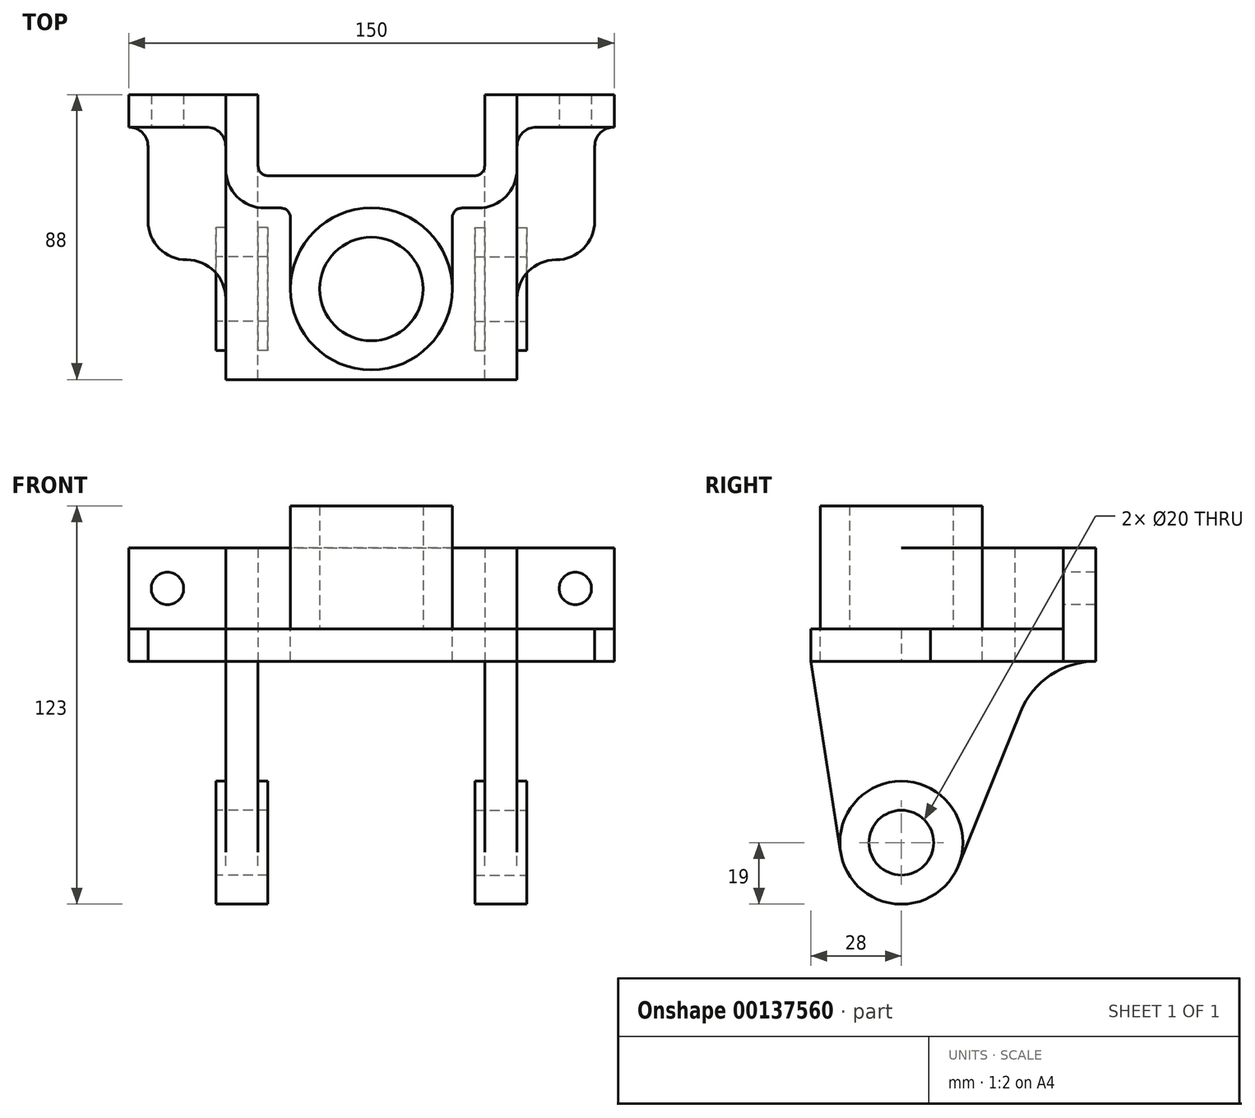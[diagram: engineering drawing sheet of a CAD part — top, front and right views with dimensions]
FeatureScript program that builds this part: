
annotation { "Feature Type Name" : "Feature", "Feature Type Description" : "" }
export const myFeature = defineFeature(function(context is Context, id is Id, definition is map)
    precondition{}
    {
        {
            var Q0;
            Q0=qCreatedBy(makeId("Top.planeOp"),FACE);
            var sketch = newSketch(context, id + "F0", { "sketchPlane" : qUnion([Q0])});
            skCircle(sketch, "E0", {"center": v(0, 0) * mm, "radius": 16 * mm});
            skCircle(sketch, "E1", {"center": v(0, 0) * mm, "radius": 25 * mm});
            skSolve(sketch);
        }
        {
            var Q0;
            Q0 = qSketchRegion(id + "F0", true);
            extrude(context, id + "F1", {"entities" : qUnion([Q0]), "depth" : 38 * mm});
        }
        {
            var Q0;
            Q0=qCreatedBy(makeId("Top.planeOp"),FACE);
            var sketch = newSketch(context, id + "F2", { "sketchPlane" : qUnion([Q0])});
            skLineSegment(sketch, "E2", {"start": v(-75, 60) * mm, "end": v(-35, 60) * mm});
            skLineSegment(sketch, "E3", {"start": v(-75, 60) * mm, "end": v(-75, 50) * mm});
            skLineSegment(sketch, "E4", {"start": v(-75, 50) * mm, "end": v(-45, 50) * mm});
            skLineSegment(sketch, "E5", {"start": v(-35, 35) * mm, "end": v(0, 35) * mm});
            skLineSegment(sketch, "E6", {"start": v(-25, 0) * mm, "end": v(-25, 25) * mm});
            skLineSegment(sketch, "E7", {"start": v(-35, 60) * mm, "end": v(-35, 35) * mm});
            skLineSegment(sketch, "E8", {"start": v(-45, 50) * mm, "end": v(-45, 25) * mm});
            skLineSegment(sketch, "E9", {"start": v(-45, 25) * mm, "end": v(-25, 25) * mm});
            skLineSegment(sketch, "E10", {"start": v(0, 56.78) * mm, "end": v(0, -59.54) * mm, "construction": true});
            skLineSegment(sketch, "E11", {"start": v(-57.64, 0) * mm, "end": v(65.58, 0) * mm, "construction": true});
            skLineSegment(sketch, "E12.MirrorCS", {"start": v(75, 60) * mm, "end": v(35, 60) * mm});
            skLineSegment(sketch, "E13.MirrorCS", {"start": v(75, 60) * mm, "end": v(75, 50) * mm});
            skLineSegment(sketch, "E14.MirrorCS", {"start": v(75, 50) * mm, "end": v(45, 50) * mm});
            skLineSegment(sketch, "E15.MirrorCS", {"start": v(35, 60) * mm, "end": v(35, 35) * mm});
            skLineSegment(sketch, "E16.MirrorCS", {"start": v(45, 50) * mm, "end": v(45, 25) * mm});
            skLineSegment(sketch, "E17.MirrorCS", {"start": v(45, 25) * mm, "end": v(25, 25) * mm});
            skLineSegment(sketch, "E18.MirrorCS", {"start": v(35, 35) * mm, "end": v(0, 35) * mm});
            skLineSegment(sketch, "E19.MirrorCS", {"start": v(25, 0) * mm, "end": v(25, 25) * mm});
            skArc(sketch, "E20.0", {"start": v(25, 0) * mm, "mid": v(0, 25) * mm, "end": v(-25, 0) * mm});
            skSolve(sketch);
        }
        {
            var Q0;
            Q0 = qSketchRegion(id + "F2", true);
            extrude(context, id + "F3", {"entities" : qUnion([Q0]), "operationType" : NewBodyOperationType.ADD, "depth" : 25 * mm, "hasSecondDirection" : true, "secondDirectionOppositeDirection" : true, "secondDirectionDepth" : 10 * mm});
        }
        {
            var Q0;
            Q0=makeQuery(id+"F3.opExtrude","SWEPT_EDGE",EDGE,{"disambiguationData":[OSD([sQuery(id+"F2.wireOp",EDGE,"E14.MirrorCS"),sQuery(id+"F2.wireOp",EDGE,"E16.MirrorCS")])]});
            var Q1;
            Q1=makeQuery(id+"F3.opExtrude","SWEPT_EDGE",EDGE,{"disambiguationData":[OSD([sQuery(id+"F2.wireOp",EDGE,"E4"),sQuery(id+"F2.wireOp",EDGE,"E8")])]});
            fillet(context, id + "F4", {"entities" : qUnion([Q0, Q1]), "radius" : 6 * mm, "tangentPropagation" : true, "allowEdgeOverflow" : false});
        }
        {
            var Q0;
            Q0=makeQuery(id+"F3.opExtrude","SWEPT_EDGE",EDGE,{"disambiguationData":[OSD([sQuery(id+"F2.wireOp",EDGE,"E17.MirrorCS"),sQuery(id+"F2.wireOp",EDGE,"E19.MirrorCS")])]});
            var Q1;
            Q1=makeQuery(id+"F3.opExtrude","SWEPT_EDGE",EDGE,{"disambiguationData":[OSD([sQuery(id+"F2.wireOp",EDGE,"E6"),sQuery(id+"F2.wireOp",EDGE,"E9")])]});
            var Q2;
            Q2=makeQuery(id+"F3.opExtrude","SWEPT_EDGE",EDGE,{"disambiguationData":[OSD([sQuery(id+"F2.wireOp",EDGE,"E5"),sQuery(id+"F2.wireOp",EDGE,"E7")])]});
            var Q3;
            Q3=makeQuery(id+"F3.opExtrude","SWEPT_EDGE",EDGE,{"disambiguationData":[OSD([sQuery(id+"F2.wireOp",EDGE,"E15.MirrorCS"),sQuery(id+"F2.wireOp",EDGE,"E18.MirrorCS")])]});
            fillet(context, id + "F5", {"entities" : qUnion([Q0, Q1, Q2, Q3]), "radius" : 3 * mm, "tangentPropagation" : true, "allowEdgeOverflow" : false});
        }
        {
            var Q0;
            Q0=makeQuery(id+"F3.opExtrude","SWEPT_EDGE",EDGE,{"disambiguationData":[OSD([sQuery(id+"F2.wireOp",EDGE,"E8"),sQuery(id+"F2.wireOp",EDGE,"E9")])]});
            var Q1;
            Q1=makeQuery(id+"F3.opExtrude","SWEPT_EDGE",EDGE,{"disambiguationData":[OSD([sQuery(id+"F2.wireOp",EDGE,"E16.MirrorCS"),sQuery(id+"F2.wireOp",EDGE,"E17.MirrorCS")])]});
            fillet(context, id + "F6", {"entities" : qUnion([Q0, Q1]), "radius" : 12 * mm, "tangentPropagation" : true, "allowEdgeOverflow" : false});
        }
        {
            var Q0;
            Q0=qCreatedBy(makeId("Top.planeOp"),FACE);
            var sketch = newSketch(context, id + "F7", { "sketchPlane" : qUnion([Q0])});
            skLineSegment(sketch, "E21", {"start": v(0, -28) * mm, "end": v(45, -28) * mm});
            skLineSegment(sketch, "E22.0", {"start": v(75, 50) * mm, "end": v(51, 50) * mm});
            skArc(sketch, "E23", {"start": v(75, 50) * mm, "mid": v(70.76, 48.24) * mm, "end": v(69, 44) * mm});
            skLineSegment(sketch, "E24", {"start": v(69, 44) * mm, "end": v(69, 9) * mm});
            skLineSegment(sketch, "E25", {"start": v(45, -28) * mm, "end": v(45, 9) * mm});
            skLineSegment(sketch, "E26", {"start": v(69, 9) * mm, "end": v(45, 9) * mm});
            skLineSegment(sketch, "E27", {"start": v(0, 64.57) * mm, "end": v(0, -62.74) * mm, "construction": true});
            skPoint(sketch, "E27.endSnap0", {"position": v(0, -28) * mm});
            skPoint(sketch, "E28.orphan", {"position": v(-45, -28) * mm});
            skLineSegment(sketch, "E29.MirrorCS", {"start": v(0, -28) * mm, "end": v(-45, -28) * mm});
            skLineSegment(sketch, "E30.MirrorCS", {"start": v(-45, -28) * mm, "end": v(-45, 9) * mm});
            skLineSegment(sketch, "E31.MirrorCS", {"start": v(-69, 9) * mm, "end": v(-45, 9) * mm});
            skLineSegment(sketch, "E32.MirrorCS", {"start": v(-69, 44) * mm, "end": v(-69, 9) * mm});
            skArc(sketch, "E33.MirrorCS", {"start": v(-75, 50) * mm, "mid": v(-70.76, 48.24) * mm, "end": v(-69, 44) * mm});
            skLineSegment(sketch, "E34.0", {"start": v(-75, 50) * mm, "end": v(-51, 50) * mm});
            skLineSegment(sketch, "E35.0", {"start": v(-45, 44) * mm, "end": v(-45, 37) * mm});
            skLineSegment(sketch, "E36.0", {"start": v(-33, 25) * mm, "end": v(-28, 25) * mm});
            skLineSegment(sketch, "E37.0", {"start": v(-25, 0) * mm, "end": v(-25, 22) * mm});
            skLineSegment(sketch, "E38.0", {"start": v(25, 0) * mm, "end": v(25, 22) * mm});
            skLineSegment(sketch, "E39.0", {"start": v(33, 25) * mm, "end": v(28, 25) * mm});
            skLineSegment(sketch, "E40.0", {"start": v(45, 44) * mm, "end": v(45, 37) * mm});
            skArc(sketch, "E41.0", {"start": v(-25, 0) * mm, "mid": v(0, -25) * mm, "end": v(25, 0) * mm});
            skArc(sketch, "E42.0", {"start": v(45, 44) * mm, "mid": v(46.76, 48.24) * mm, "end": v(51, 50) * mm});
            skArc(sketch, "E43.0", {"start": v(25, 22) * mm, "mid": v(25.88, 24.12) * mm, "end": v(28, 25) * mm});
            skArc(sketch, "E44.0", {"start": v(-28, 25) * mm, "mid": v(-25.88, 24.12) * mm, "end": v(-25, 22) * mm});
            skArc(sketch, "E45.0", {"start": v(-51, 50) * mm, "mid": v(-46.76, 48.24) * mm, "end": v(-45, 44) * mm});
            skPoint(sketch, "E46.orphan", {"position": v(-45, 50) * mm});
            skPoint(sketch, "E47.orphan", {"position": v(-25, 25) * mm});
            skPoint(sketch, "E48.orphan", {"position": v(25, 25) * mm});
            skPoint(sketch, "E49.orphan", {"position": v(45, 50) * mm});
            skArc(sketch, "E50.0", {"start": v(-45, 37) * mm, "mid": v(-41.49, 28.51) * mm, "end": v(-33, 25) * mm});
            skArc(sketch, "E51.0", {"start": v(33, 25) * mm, "mid": v(41.49, 28.51) * mm, "end": v(45, 37) * mm});
            skSolve(sketch);
        }
        {
            var Q0;
            Q0 = qSketchRegion(id + "F7", true);
            extrude(context, id + "F8", {"entities" : qUnion([Q0]), "oppositeDirection" : true, "depth" : 10 * mm});
        }
        {
            var Q0;
            Q0=makeQuery(id+"F8.opExtrude","SWEPT_EDGE",EDGE,{"disambiguationData":[OSD([sQuery(id+"F7.wireOp",EDGE,"E31.MirrorCS"),sQuery(id+"F7.wireOp",EDGE,"E32.MirrorCS")])]});
            var Q1;
            Q1=makeQuery(id+"F8.opExtrude","SWEPT_EDGE",EDGE,{"disambiguationData":[OSD([sQuery(id+"F7.wireOp",EDGE,"E30.MirrorCS"),sQuery(id+"F7.wireOp",EDGE,"E31.MirrorCS")])]});
            var Q2;
            Q2=makeQuery(id+"F8.opExtrude","SWEPT_EDGE",EDGE,{"disambiguationData":[OSD([sQuery(id+"F7.wireOp",EDGE,"E25"),sQuery(id+"F7.wireOp",EDGE,"E26")])]});
            var Q3;
            Q3=makeQuery(id+"F8.opExtrude","SWEPT_EDGE",EDGE,{"disambiguationData":[OSD([sQuery(id+"F7.wireOp",EDGE,"E24"),sQuery(id+"F7.wireOp",EDGE,"E26")])]});
            fillet(context, id + "F9", {"entities" : qUnion([Q0, Q1, Q2, Q3]), "radius" : 12 * mm, "tangentPropagation" : true, "allowEdgeOverflow" : false});
        }
        {
            var Q0;
            Q0=makeQuery(id+"F8.opExtrude","SWEPT_FACE",FACE,{"disambiguationData":[OSD([sQuery(id+"F7.wireOp",EDGE,"E25")])]});
            var sketch = newSketch(context, id + "F10", { "sketchPlane" : qUnion([Q0])});
            skArc(sketch, "E52", {"start": v(-18.77, -68.94) * mm, "mid": v(-2.17, -84.88) * mm, "end": v(17.61, -73.12) * mm});
            skLineSegment(sketch, "E53.0", {"start": v(-28, -10) * mm, "end": v(-3, -10) * mm});
            skLineSegment(sketch, "E54", {"start": v(-28, -10) * mm, "end": v(-18.77, -68.94) * mm});
            skArc(sketch, "E55", {"start": v(60, -10) * mm, "mid": v(46.02, -14.27) * mm, "end": v(36.82, -25.63) * mm});
            skLineSegment(sketch, "E56", {"start": v(17.61, -73.12) * mm, "end": v(36.82, -25.63) * mm});
            skLineSegment(sketch, "E57.0", {"start": v(9, -10) * mm, "end": v(-3, -10) * mm});
            skLineSegment(sketch, "E58.0", {"start": v(21, -10) * mm, "end": v(9, -10) * mm});
            skLineSegment(sketch, "E59.0", {"start": v(44, -10) * mm, "end": v(21, -10) * mm});
            skLineSegment(sketch, "E60.0", {"start": v(50, -10) * mm, "end": v(44, -10) * mm});
            skLineSegment(sketch, "E61.0", {"start": v(60, -10) * mm, "end": v(50, -10) * mm});
            skSolve(sketch);
        }
        {
            var Q0;
            Q0 = qSketchRegion(id + "F10", true);
            extrude(context, id + "F11", {"entities" : qUnion([Q0]), "oppositeDirection" : true, "depth" : 10 * mm});
        }
        {
            var Q0;
            Q0=makeQuery(id+"F11.opExtrude","CAP_FACE",FACE,{"disambiguationData":[OSD([sQuery(id+"F10.wireOp",EDGE,"E52"),sQuery(id+"F10.wireOp",EDGE,"E53.0"),sQuery(id+"F10.wireOp",EDGE,"E54"),sQuery(id+"F10.wireOp",EDGE,"E55"),sQuery(id+"F10.wireOp",EDGE,"E56"),sQuery(id+"F10.wireOp",EDGE,"E57.0"),sQuery(id+"F10.wireOp",EDGE,"E58.0"),sQuery(id+"F10.wireOp",EDGE,"E59.0"),sQuery(id+"F10.wireOp",EDGE,"E60.0"),sQuery(id+"F10.wireOp",EDGE,"E61.0")])],"isStart":true});
            var sketch = newSketch(context, id + "F12", { "sketchPlane" : qUnion([Q0])});
            skCircle(sketch, "E62", {"center": v(0, -66) * mm, "radius": 19 * mm});
            skSolve(sketch);
        }
        {
            var Q0;
            Q0 = qSketchRegion(id + "F12", true);
            extrude(context, id + "F13", {"entities" : qUnion([Q0]), "depth" : 3 * mm});
        }
        {
            var Q0;
            Q0=makeQuery(id+"F13.opExtrude","CAP_FACE",FACE,{"disambiguationData":[OSD([sQuery(id+"F12.wireOp",EDGE,"E62")])],"isStart":false});
            cPlane(context, id + "F14", {"entities" : qUnion([Q0]), "cplaneType" : CPlaneType.OFFSET, "offset" : 8 * mm, "oppositeDirection" : true, "width" : 150 * mm, "height" : 150 * mm});
        }
        {
            var Q0;
            Q0=makeQuery(id+"F13.opExtrude","SWEPT_BODY",BODY,{"disambiguationData":[OSD([sQuery(id+"F12.wireOp",EDGE,"E62")])]});
            var Q1;
            Q1=qCreatedBy(id+"F14.planeOp",FACE);
            mirror(context, id + "F15", {"operationType" : NewBodyOperationType.ADD, "entities" : qUnion([Q0]), "mirrorPlane" : qUnion([Q1])});
        }
        {
            var Q0;
            Q0=makeQuery(id+"F13.opExtrude","CAP_FACE",FACE,{"disambiguationData":[OSD([sQuery(id+"F12.wireOp",EDGE,"E62")])],"isStart":false});
            var sketch = newSketch(context, id + "F16", { "sketchPlane" : qUnion([Q0])});
            skPoint(sketch, "E63", {"position": v(0, -66) * mm});
            skSolve(sketch);
        }
        {
            var Q0;
            Q0=sQuery(id+"F16.wireOp",VERTEX,"E63");
            var Q1;
            Q1=makeQuery(id+"F11.opExtrude","SWEPT_BODY",BODY,{"disambiguationData":[OSD([sQuery(id+"F10.wireOp",EDGE,"E52"),sQuery(id+"F10.wireOp",EDGE,"E53.0"),sQuery(id+"F10.wireOp",EDGE,"E54"),sQuery(id+"F10.wireOp",EDGE,"E55"),sQuery(id+"F10.wireOp",EDGE,"E56"),sQuery(id+"F10.wireOp",EDGE,"E57.0"),sQuery(id+"F10.wireOp",EDGE,"E58.0"),sQuery(id+"F10.wireOp",EDGE,"E59.0"),sQuery(id+"F10.wireOp",EDGE,"E60.0"),sQuery(id+"F10.wireOp",EDGE,"E61.0")])]});
            hole(context, id + "F17", {"style" : HoleStyle.SIMPLE, "endStyle" : HoleEndStyle.BLIND, "holeDiameter" : 20 * mm, "holeDepth" : 25 * mm, "locations" : qUnion([Q0]), "scope" : qUnion([Q1])});
        }
        {
            var Q0;
            Q0=makeQuery(id+"F11.opExtrude","SWEPT_BODY",BODY,{"disambiguationData":[OSD([sQuery(id+"F10.wireOp",EDGE,"E52"),sQuery(id+"F10.wireOp",EDGE,"E53.0"),sQuery(id+"F10.wireOp",EDGE,"E54"),sQuery(id+"F10.wireOp",EDGE,"E55"),sQuery(id+"F10.wireOp",EDGE,"E56"),sQuery(id+"F10.wireOp",EDGE,"E57.0"),sQuery(id+"F10.wireOp",EDGE,"E58.0"),sQuery(id+"F10.wireOp",EDGE,"E59.0"),sQuery(id+"F10.wireOp",EDGE,"E60.0"),sQuery(id+"F10.wireOp",EDGE,"E61.0")])]});
            var Q1;
            Q1=qCreatedBy(makeId("Right.planeOp"),FACE);
            mirror(context, id + "F18", {"entities" : qUnion([Q0]), "mirrorPlane" : qUnion([Q1])});
        }
        {
            var Q0;
            Q0=makeQuery(id+"F3.opExtrude","SWEPT_FACE",FACE,{"disambiguationData":[OSD([sQuery(id+"F2.wireOp",EDGE,"E14.MirrorCS")])]});
            var sketch = newSketch(context, id + "F19", { "sketchPlane" : qUnion([Q0])});
            skPoint(sketch, "E64", {"position": v(63, 12.5) * mm});
            skPoint(sketch, "E65.MirrorP", {"position": v(-63, 12.5) * mm});
            skSolve(sketch);
        }
        {
            var Q0;
            Q0=sQuery(id+"F19.wireOp",VERTEX,"E65.MirrorP");
            var Q1;
            Q1=sQuery(id+"F19.wireOp",VERTEX,"E64");
            var Q2;
            Q2=makeQuery(id+"F1.opExtrude","SWEPT_BODY",BODY,{"disambiguationData":[OSD([sQuery(id+"F0.wireOp",EDGE,"E0"),sQuery(id+"F0.wireOp",EDGE,"E1")])]});
            hole(context, id + "F20", {"style" : HoleStyle.SIMPLE, "endStyle" : HoleEndStyle.BLIND, "holeDiameter" : 10 * mm, "holeDepth" : 25 * mm, "locations" : qUnion([Q0, Q1]), "scope" : qUnion([Q2])});
        }
    });
